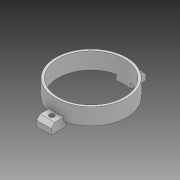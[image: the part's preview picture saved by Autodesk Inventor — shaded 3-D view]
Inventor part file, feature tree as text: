
AUTODESK INVENTOR PART (.ipt)
format: ipt  version: 2018 (Build 220112000, 112)  size: 146,432 bytes
history: native  units: mm
features: extrude x4, sketch x4, chamfer x2, other x1
ambient origin geometry x8: Origin, YZ Plane, XZ Plane, XY Plane, X Axis, Y Axis, Z Axis, Center Point
bodies: Body1 (feature_tree)
feature tree (11):
  other  "ソリッド1"
  extrude  "押し出し1"  Depth=18.0mm
  chamfer  "面取り1"  Distance=18.0mm
  extrude  "押し出し2"  Depth=51.5mm
  extrude  "押し出し3"  Depth=25.75mm
  chamfer  "面取り2"  Distance=8.0mm
  extrude  "押し出し4"  Depth=5.0mm TaperAngle=0.0deg
  sketch  "スケッチ1"
  sketch  "スケッチ2"
  sketch  "スケッチ3"
  sketch  "スケッチ4"
